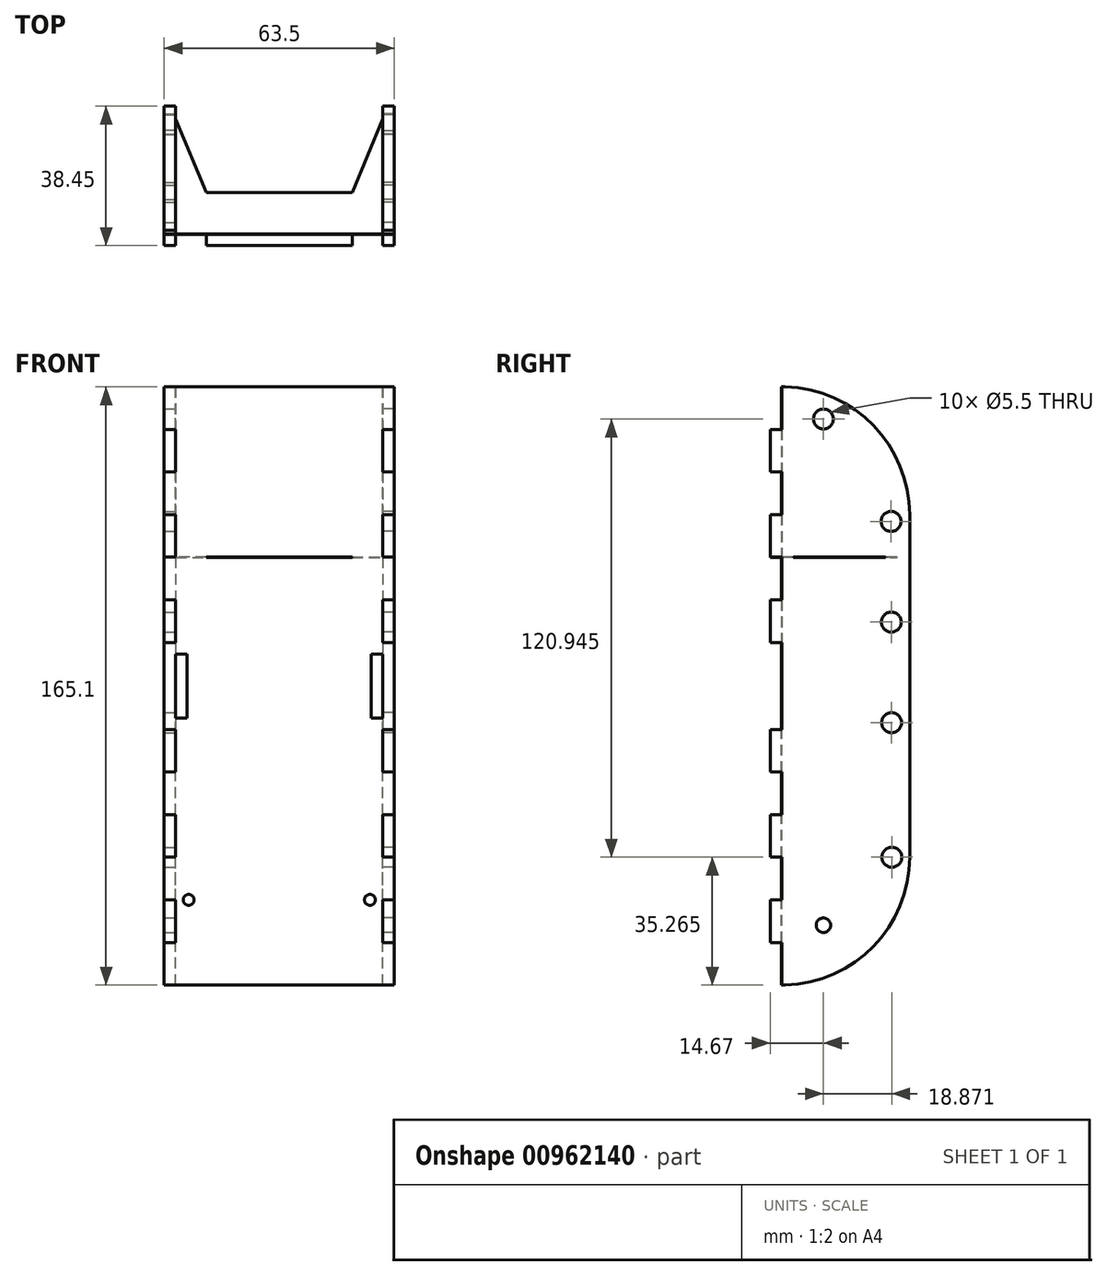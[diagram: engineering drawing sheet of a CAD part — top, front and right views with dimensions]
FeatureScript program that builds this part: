
annotation { "Feature Type Name" : "Feature", "Feature Type Description" : "" }
export const myFeature = defineFeature(function(context is Context, id is Id, definition is map)
    precondition{}
    {
        {
            assignVariable(context, id + "F0", {"name" : "Thickness", "anyValue" : .125});
        }
        {
            var Q0;
            Q0=qCreatedBy(makeId("Front.planeOp"),FACE);
            var sketch = newSketch(context, id + "F1", { "sketchPlane" : qUnion([Q0])});
            skLineSegment(sketch, "E0", {"start": v(0, 0) * mm, "end": v(0, 49.56) * mm, "construction": true});
            skLineSegment(sketch, "E1", {"start": v(0, 0) * mm, "end": v(-25, 0) * mm, "construction": true});
            skCircle(sketch, "E2", {"center": v(-25, 0) * mm, "radius": 1.5 * mm, "construction": true});
            skLineSegment(sketch, "E3", {"start": v(0, -7) * mm, "end": v(-39.83, -7) * mm, "construction": true});
            skLineSegment(sketch, "E4", {"start": v(0, 141.6) * mm, "end": v(-22.22, 141.6) * mm, "construction": true});
            skLineSegment(sketch, "E5", {"start": v(-22.23, 141.6) * mm, "end": v(-22.22, -23.51) * mm, "construction": true});
            skLineSegment(sketch, "E6", {"start": v(-22.22, -23.51) * mm, "end": v(0, -23.5) * mm, "construction": true});
            skSolve(sketch);
        }
        {
            var Q0;
            Q0=qCreatedBy(makeId("Right.planeOp"),FACE);
            var sketch = newSketch(context, id + "F2", { "sketchPlane" : qUnion([Q0])});
            skLineSegment(sketch, "E7", {"start": v(0, -7) * mm, "end": v(11.5, -7) * mm, "construction": true});
            skCircle(sketch, "E8", {"center": v(11.5, -7) * mm, "radius": 2 * mm});
            skCircle(sketch, "E9", {"center": v(11.5, 132.7) * mm, "radius": 2.75 * mm});
            skSolve(sketch);
        }
        {
            var Q0;
            Q0=qCreatedBy(makeId("Front.planeOp"),FACE);
            var sketch = newSketch(context, id + "F3", { "sketchPlane" : qUnion([Q0])});
            skLineSegment(sketch, "E10", {"start": v(0, 141.6) * mm, "end": v(-31.75, 141.6) * mm, "construction": true});
            skLineSegment(sketch, "E11", {"start": v(0, -23.51) * mm, "end": v(-31.75, -23.51) * mm});
            skLineSegment(sketch, "E12", {"start": v(-31.75, -23.51) * mm, "end": v(-31.75, -11.76) * mm});
            skLineSegment(sketch, "E13", {"start": v(-31.75, -11.76) * mm, "end": v(-28.57, -11.76) * mm});
            skLineSegment(sketch, "E14", {"start": v(-28.57, -11.76) * mm, "end": v(-28.57, 0) * mm});
            skLineSegment(sketch, "E15", {"start": v(-28.57, 0) * mm, "end": v(-31.75, 0) * mm});
            skLineSegment(sketch, "E16", {"start": v(0, -23.51) * mm, "end": v(0, 141.6) * mm, "construction": true});
            skLineSegment(sketch, "E17", {"start": v(0, 59.04) * mm, "end": v(-66.34, 59.04) * mm, "construction": true});
            skLineSegment(sketch, "E18", {"start": v(-31.75, 59.04) * mm, "end": v(-31.75, 47.02) * mm});
            skLineSegment(sketch, "E19.1.0.0", {"start": v(-28.57, 23.51) * mm, "end": v(-31.75, 23.51) * mm});
            skLineSegment(sketch, "E19.1.0.1", {"start": v(-28.57, 11.76) * mm, "end": v(-28.57, 23.51) * mm});
            skLineSegment(sketch, "E19.1.0.2", {"start": v(-31.75, 11.76) * mm, "end": v(-28.57, 11.76) * mm});
            skLineSegment(sketch, "E19.1.0.3", {"start": v(-31.75, 0) * mm, "end": v(-31.75, 11.76) * mm});
            skLineSegment(sketch, "E19.2.0.0", {"start": v(-28.58, 47.02) * mm, "end": v(-31.75, 47.02) * mm});
            skLineSegment(sketch, "E19.2.0.1", {"start": v(-28.57, 35.27) * mm, "end": v(-28.57, 47.02) * mm});
            skLineSegment(sketch, "E19.2.0.2", {"start": v(-31.75, 35.27) * mm, "end": v(-28.58, 35.27) * mm});
            skLineSegment(sketch, "E19.2.0.3", {"start": v(-31.75, 23.51) * mm, "end": v(-31.75, 35.27) * mm});
            skLineSegment(sketch, "E19.direction1", {"start": v(-31.75, -23.51) * mm, "end": v(-31.75, 0) * mm, "construction": true});
            skLineSegment(sketch, "E20.MirrorCS", {"start": v(-31.75, 141.6) * mm, "end": v(-31.75, 129.84) * mm});
            skLineSegment(sketch, "E21.MirrorCS", {"start": v(-28.57, 118.08) * mm, "end": v(-31.75, 118.08) * mm});
            skLineSegment(sketch, "E22.MirrorCS", {"start": v(-28.58, 71.06) * mm, "end": v(-31.75, 71.06) * mm});
            skLineSegment(sketch, "E23.MirrorCS", {"start": v(-31.75, 94.57) * mm, "end": v(-31.75, 82.81) * mm});
            skLineSegment(sketch, "E24.MirrorCS", {"start": v(-31.75, 118.08) * mm, "end": v(-31.75, 106.33) * mm});
            skLineSegment(sketch, "E25.MirrorCS", {"start": v(-31.75, 129.84) * mm, "end": v(-28.57, 129.84) * mm});
            skLineSegment(sketch, "E26.MirrorCS", {"start": v(-28.57, 129.84) * mm, "end": v(-28.57, 118.08) * mm});
            skLineSegment(sketch, "E27.MirrorCS", {"start": v(-28.57, 82.81) * mm, "end": v(-28.57, 71.06) * mm});
            skLineSegment(sketch, "E28.MirrorCS", {"start": v(-31.75, 82.81) * mm, "end": v(-28.58, 82.81) * mm});
            skLineSegment(sketch, "E29.MirrorCS", {"start": v(-31.75, 106.33) * mm, "end": v(-28.57, 106.33) * mm});
            skLineSegment(sketch, "E30.MirrorCS", {"start": v(-28.57, 106.33) * mm, "end": v(-28.57, 94.57) * mm});
            skLineSegment(sketch, "E31.MirrorCS", {"start": v(-28.57, 94.57) * mm, "end": v(-31.75, 94.57) * mm});
            skLineSegment(sketch, "E32.MirrorCS", {"start": v(0, 141.6) * mm, "end": v(-31.75, 141.6) * mm});
            skLineSegment(sketch, "E33.MirrorCS", {"start": v(-31.75, 59.04) * mm, "end": v(-31.75, 71.06) * mm});
            skLineSegment(sketch, "E34.bottom", {"start": v(-28.58, 67.89) * mm, "end": v(-25.4, 67.89) * mm});
            skLineSegment(sketch, "E34.top", {"start": v(-28.58, 50.2) * mm, "end": v(-25.4, 50.2) * mm});
            skLineSegment(sketch, "E34.left", {"start": v(-28.58, 67.89) * mm, "end": v(-28.58, 50.2) * mm});
            skLineSegment(sketch, "E34.right", {"start": v(-25.4, 67.89) * mm, "end": v(-25.4, 50.2) * mm});
            skPoint(sketch, "E35", {"position": v(-28.58, 59.04) * mm});
            skLineSegment(sketch, "E36.MirrorCS", {"start": v(28.57, 23.51) * mm, "end": v(31.75, 23.51) * mm});
            skLineSegment(sketch, "E37.MirrorCS", {"start": v(31.75, 35.27) * mm, "end": v(28.58, 35.27) * mm});
            skLineSegment(sketch, "E38.MirrorCS", {"start": v(28.58, 71.06) * mm, "end": v(31.75, 71.06) * mm});
            skLineSegment(sketch, "E39.MirrorCS", {"start": v(31.75, -23.51) * mm, "end": v(31.75, -11.76) * mm});
            skLineSegment(sketch, "E40.MirrorCS", {"start": v(28.57, 0) * mm, "end": v(31.75, 0) * mm});
            skLineSegment(sketch, "E41.MirrorCS", {"start": v(28.58, 67.89) * mm, "end": v(25.4, 67.89) * mm});
            skLineSegment(sketch, "E42.MirrorCS", {"start": v(31.75, 82.81) * mm, "end": v(28.58, 82.81) * mm});
            skLineSegment(sketch, "E43.MirrorCS", {"start": v(31.75, 59.04) * mm, "end": v(31.75, 71.06) * mm});
            skLineSegment(sketch, "E44.MirrorCS", {"start": v(31.75, 11.76) * mm, "end": v(28.57, 11.76) * mm});
            skLineSegment(sketch, "E45.MirrorCS", {"start": v(31.75, 94.57) * mm, "end": v(31.75, 82.81) * mm});
            skLineSegment(sketch, "E46.MirrorCS", {"start": v(31.75, 141.6) * mm, "end": v(31.75, 129.84) * mm});
            skLineSegment(sketch, "E47.MirrorCS", {"start": v(28.57, 94.57) * mm, "end": v(31.75, 94.57) * mm});
            skLineSegment(sketch, "E48.MirrorCS", {"start": v(31.75, 118.08) * mm, "end": v(31.75, 106.33) * mm});
            skLineSegment(sketch, "E49.MirrorCS", {"start": v(31.75, -11.76) * mm, "end": v(28.57, -11.76) * mm});
            skLineSegment(sketch, "E50.MirrorCS", {"start": v(28.57, 118.08) * mm, "end": v(31.75, 118.08) * mm});
            skLineSegment(sketch, "E51.MirrorCS", {"start": v(31.75, 23.51) * mm, "end": v(31.75, 35.27) * mm});
            skLineSegment(sketch, "E52.MirrorCS", {"start": v(28.57, -11.76) * mm, "end": v(28.57, 0) * mm});
            skLineSegment(sketch, "E53.MirrorCS", {"start": v(31.75, 129.84) * mm, "end": v(28.57, 129.84) * mm});
            skLineSegment(sketch, "E54.MirrorCS", {"start": v(28.58, 67.89) * mm, "end": v(28.58, 50.2) * mm});
            skLineSegment(sketch, "E55.MirrorCS", {"start": v(28.58, 47.02) * mm, "end": v(31.75, 47.02) * mm});
            skLineSegment(sketch, "E56.MirrorCS", {"start": v(28.57, 35.27) * mm, "end": v(28.57, 47.02) * mm});
            skLineSegment(sketch, "E57.MirrorCS", {"start": v(31.75, 0) * mm, "end": v(31.75, 11.76) * mm});
            skLineSegment(sketch, "E58.MirrorCS", {"start": v(31.75, 59.04) * mm, "end": v(31.75, 47.02) * mm});
            skLineSegment(sketch, "E59.MirrorCS", {"start": v(28.57, 11.76) * mm, "end": v(28.57, 23.51) * mm});
            skLineSegment(sketch, "E60.MirrorCS", {"start": v(28.58, 50.2) * mm, "end": v(25.4, 50.2) * mm});
            skLineSegment(sketch, "E61.MirrorCS", {"start": v(31.75, 106.33) * mm, "end": v(28.57, 106.33) * mm});
            skLineSegment(sketch, "E62.MirrorCS", {"start": v(28.57, 82.81) * mm, "end": v(28.57, 71.06) * mm});
            skLineSegment(sketch, "E63.MirrorCS", {"start": v(28.57, 129.84) * mm, "end": v(28.57, 118.08) * mm});
            skLineSegment(sketch, "E64.MirrorCS", {"start": v(28.57, 106.33) * mm, "end": v(28.57, 94.57) * mm});
            skLineSegment(sketch, "E65.MirrorCS", {"start": v(0, 141.6) * mm, "end": v(31.75, 141.6) * mm});
            skLineSegment(sketch, "E66.MirrorCS", {"start": v(25.4, 67.89) * mm, "end": v(25.4, 50.2) * mm});
            skLineSegment(sketch, "E67.MirrorCS", {"start": v(0, 141.6) * mm, "end": v(31.75, 141.6) * mm, "construction": true});
            skLineSegment(sketch, "E68.MirrorCS", {"start": v(0, -23.51) * mm, "end": v(31.75, -23.51) * mm});
            skPoint(sketch, "E69.MirrorP", {"position": v(28.58, 59.04) * mm});
            skCircle(sketch, "E70", {"center": v(-25, 0) * mm, "radius": 1.5 * mm});
            skCircle(sketch, "E71.MirrorC", {"center": v(25, 0) * mm, "radius": 1.5 * mm});
            skSolve(sketch);
        }
        {
            var Q0;
            Q0=makeQuery(id+"F3.imprint","IMPRINT",FACE,{"disambiguationData":[TD([[makeQuery(id+"F3.imprint","IMPRINT",EDGE,{"derivedFrom":sQuery(id+"F3.wireOp",EDGE,"E11")}),-1.0]])]});
            extrude(context, id + "F4", {"entities" : qUnion([Q0]), "depth" : (getVariable(context, 'Thickness')) * mm, "offsetDistance" : 25.4 * mm});
        }
        {
            var Q0;
            Q0=qCreatedBy(makeId("Right.planeOp"),FACE);
            var sketch = newSketch(context, id + "F5", { "sketchPlane" : qUnion([Q0])});
            skLineSegment(sketch, "E72", {"start": v(0, -23.51) * mm, "end": v(0, -11.76) * mm});
            skLineSegment(sketch, "E73", {"start": v(0, -11.76) * mm, "end": v(-3.18, -11.76) * mm});
            skLineSegment(sketch, "E74", {"start": v(-3.18, -11.76) * mm, "end": v(-3.18, 0) * mm});
            skLineSegment(sketch, "E75", {"start": v(-3.18, 0) * mm, "end": v(0, 0) * mm});
            skLineSegment(sketch, "E76.1.0.0", {"start": v(0, 0) * mm, "end": v(0, 11.75) * mm});
            skLineSegment(sketch, "E76.1.0.1", {"start": v(0, 11.76) * mm, "end": v(-3.18, 11.75) * mm});
            skLineSegment(sketch, "E76.1.0.2", {"start": v(-3.18, 11.75) * mm, "end": v(-3.18, 23.51) * mm});
            skLineSegment(sketch, "E76.1.0.3", {"start": v(-3.18, 23.51) * mm, "end": v(0, 23.51) * mm});
            skLineSegment(sketch, "E76.2.0.0", {"start": v(0, 23.51) * mm, "end": v(0, 35.27) * mm});
            skLineSegment(sketch, "E76.2.0.1", {"start": v(0, 35.27) * mm, "end": v(-3.17, 35.27) * mm});
            skLineSegment(sketch, "E76.2.0.2", {"start": v(-3.17, 35.27) * mm, "end": v(-3.17, 47.02) * mm});
            skLineSegment(sketch, "E76.2.0.3", {"start": v(-3.17, 47.02) * mm, "end": v(0, 47.02) * mm});
            skLineSegment(sketch, "E76.direction1", {"start": v(0, -23.51) * mm, "end": v(0, 0) * mm, "construction": true});
            skLineSegment(sketch, "E77", {"start": v(-17.44, 59.04) * mm, "end": v(0, 59.04) * mm, "construction": true});
            skLineSegment(sketch, "E78", {"start": v(0, 47.02) * mm, "end": v(0, 59.04) * mm});
            skLineSegment(sketch, "E79.MirrorCS", {"start": v(-3.18, 118.08) * mm, "end": v(0, 118.08) * mm});
            skLineSegment(sketch, "E80.MirrorCS", {"start": v(0, 82.82) * mm, "end": v(-3.17, 82.82) * mm});
            skLineSegment(sketch, "E81.MirrorCS", {"start": v(-3.18, 94.57) * mm, "end": v(0, 94.57) * mm});
            skLineSegment(sketch, "E82.MirrorCS", {"start": v(0, 129.84) * mm, "end": v(-3.18, 129.84) * mm});
            skLineSegment(sketch, "E83.MirrorCS", {"start": v(-3.17, 71.06) * mm, "end": v(0, 71.06) * mm});
            skLineSegment(sketch, "E84.MirrorCS", {"start": v(0, 106.33) * mm, "end": v(-3.18, 106.33) * mm});
            skLineSegment(sketch, "E85.MirrorCS", {"start": v(0, 141.6) * mm, "end": v(0, 129.84) * mm});
            skLineSegment(sketch, "E86.MirrorCS", {"start": v(0, 141.6) * mm, "end": v(0, 118.08) * mm, "construction": true});
            skLineSegment(sketch, "E87.MirrorCS", {"start": v(-3.18, 106.33) * mm, "end": v(-3.18, 94.57) * mm});
            skLineSegment(sketch, "E88.MirrorCS", {"start": v(0, 118.08) * mm, "end": v(0, 106.33) * mm});
            skLineSegment(sketch, "E89.MirrorCS", {"start": v(-3.17, 82.82) * mm, "end": v(-3.17, 71.06) * mm});
            skLineSegment(sketch, "E90.MirrorCS", {"start": v(0, 71.06) * mm, "end": v(0, 59.04) * mm});
            skLineSegment(sketch, "E91.MirrorCS", {"start": v(0, 94.57) * mm, "end": v(0, 82.82) * mm});
            skLineSegment(sketch, "E92.MirrorCS", {"start": v(-3.18, 129.84) * mm, "end": v(-3.18, 118.08) * mm});
            skCircle(sketch, "E93", {"center": v(11.5, 132.7) * mm, "radius": 2.75 * mm});
            skCircle(sketch, "E94", {"center": v(11.5, -7) * mm, "radius": 2 * mm});
            skCircle(sketch, "E95", {"center": v(11.5, 132.7) * mm, "radius": 16 * mm, "construction": true});
            skCircle(sketch, "E96", {"center": v(11.5, -7) * mm, "radius": 16 * mm, "construction": true});
            skCircle(sketch, "E97", {"center": v(30.37, 21.12) * mm, "radius": 11 * mm, "construction": true});
            skCircle(sketch, "E98", {"center": v(30.16, 104.44) * mm, "radius": 11 * mm, "construction": true});
            skLineSegment(sketch, "E99", {"start": v(41.16, 104.47) * mm, "end": v(41.37, 21.15) * mm, "construction": true});
            skCircle(sketch, "E100.1.0.0", {"center": v(30.23, 76.67) * mm, "radius": 11 * mm, "construction": true});
            skCircle(sketch, "E100.2.0.0", {"center": v(30.3, 48.9) * mm, "radius": 11 * mm, "construction": true});
            skLineSegment(sketch, "E100.direction1", {"start": v(30.16, 104.44) * mm, "end": v(30.23, 76.67) * mm, "construction": true});
            skCircle(sketch, "E101", {"center": v(30.16, 104.44) * mm, "radius": 2.75 * mm});
            skCircle(sketch, "E102", {"center": v(30.23, 76.67) * mm, "radius": 2.75 * mm});
            skCircle(sketch, "E103", {"center": v(30.3, 48.9) * mm, "radius": 2.75 * mm});
            skArc(sketch, "E104", {"start": v(0.97, -23.51) * mm, "mid": v(25.29, -12.85) * mm, "end": v(35.28, 11.75) * mm});
            skArc(sketch, "E105.MirrorCS", {"start": v(0.97, 141.6) * mm, "mid": v(25.29, 130.93) * mm, "end": v(35.28, 106.33) * mm});
            skLineSegment(sketch, "E106", {"start": v(35.28, 11.76) * mm, "end": v(35.28, 106.33) * mm});
            skLineSegment(sketch, "E107", {"start": v(0.97, 141.6) * mm, "end": v(0, 141.6) * mm});
            skLineSegment(sketch, "E108", {"start": v(0.97, -23.51) * mm, "end": v(0, -23.51) * mm});
            skLineSegment(sketch, "E109", {"start": v(26.06, 139.33) * mm, "end": v(40.92, 106.72) * mm, "construction": true});
            skLineSegment(sketch, "E110", {"start": v(39.72, 15.32) * mm, "end": v(25.97, -13.82) * mm, "construction": true});
            skCircle(sketch, "E111", {"center": v(30.37, 11.76) * mm, "radius": 2.75 * mm});
            skLineSegment(sketch, "E112", {"start": v(35.28, 11.75) * mm, "end": v(0, 11.75) * mm, "construction": true});
            skLineSegment(sketch, "E113", {"start": v(33.3, 11.76) * mm, "end": v(44.3, 11.8) * mm, "construction": true});
            skArc(sketch, "E114", {"start": v(44.3, 11.8) * mm, "mid": v(16.45, 12.05) * mm, "end": v(44.28, 11.13) * mm, "construction": true});
            skSolve(sketch);
        }
        {
            var Q0;
            Q0=makeQuery(id+"F5.imprint","IMPRINT",FACE,{"disambiguationData":[TD([[makeQuery(id+"F5.imprint","IMPRINT",EDGE,{"derivedFrom":sQuery(id+"F5.wireOp",EDGE,"E72")}),-1.0]])]});
            var Q1;
            Q1=makeQuery(id+"F4.opExtrude","CAP_VERTEX",VERTEX,{"disambiguationData":[OSD([sQuery(id+"F3.wireOp",EDGE,"E46.MirrorCS"),sQuery(id+"F3.wireOp",EDGE,"E65.MirrorCS")])],"isStart":false});
            var Q2;
            Q2=makeQuery(id+"F4.opExtrude","CAP_VERTEX",VERTEX,{"disambiguationData":[OSD([sQuery(id+"F3.wireOp",EDGE,"E53.MirrorCS"),sQuery(id+"F3.wireOp",EDGE,"E63.MirrorCS")])],"isStart":true});
            extrude(context, id + "F6", {"entities" : qUnion([Q0]), "endBound" : BoundingType.UP_TO_VERTEX, "depth" : 25.4 * mm, "endBoundEntityVertex" : qUnion([Q1]), "offsetDistance" : 25.4 * mm, "hasSecondDirection" : true, "secondDirectionBound" : SecondDirectionBoundingType.UP_TO_VERTEX, "secondDirectionOppositeDirection" : false, "secondDirectionDepth" : 25.4 * mm, "secondDirectionBoundEntityVertex" : qUnion([Q2])});
        }
        {
            var Q0;
            Q0=makeQuery(id+"F6.opExtrude","SWEPT_BODY",BODY,{"disambiguationData":[OSD([sQuery(id+"F5.wireOp",EDGE,"E72"),sQuery(id+"F5.wireOp",EDGE,"E73"),sQuery(id+"F5.wireOp",EDGE,"E74"),sQuery(id+"F5.wireOp",EDGE,"E75"),sQuery(id+"F5.wireOp",EDGE,"E76.1.0.0"),sQuery(id+"F5.wireOp",EDGE,"E76.1.0.1"),sQuery(id+"F5.wireOp",EDGE,"E76.1.0.2"),sQuery(id+"F5.wireOp",EDGE,"E76.1.0.3"),sQuery(id+"F5.wireOp",EDGE,"E76.2.0.0"),sQuery(id+"F5.wireOp",EDGE,"E76.2.0.1"),sQuery(id+"F5.wireOp",EDGE,"E76.2.0.2"),sQuery(id+"F5.wireOp",EDGE,"E76.2.0.3"),sQuery(id+"F5.wireOp",EDGE,"E78"),sQuery(id+"F5.wireOp",EDGE,"E79.MirrorCS"),sQuery(id+"F5.wireOp",EDGE,"E80.MirrorCS"),sQuery(id+"F5.wireOp",EDGE,"E81.MirrorCS"),sQuery(id+"F5.wireOp",EDGE,"E82.MirrorCS"),sQuery(id+"F5.wireOp",EDGE,"E83.MirrorCS"),sQuery(id+"F5.wireOp",EDGE,"E84.MirrorCS"),sQuery(id+"F5.wireOp",EDGE,"E85.MirrorCS"),sQuery(id+"F5.wireOp",EDGE,"E87.MirrorCS"),sQuery(id+"F5.wireOp",EDGE,"E88.MirrorCS"),sQuery(id+"F5.wireOp",EDGE,"E89.MirrorCS"),sQuery(id+"F5.wireOp",EDGE,"E90.MirrorCS"),sQuery(id+"F5.wireOp",EDGE,"E91.MirrorCS"),sQuery(id+"F5.wireOp",EDGE,"E92.MirrorCS"),sQuery(id+"F5.wireOp",EDGE,"0A0D79Jb-YNL0-oHs5-xmzd-RRcL05y1tXJ9"),sQuery(id+"F5.wireOp",EDGE,"80kzLmsw-Zs1p-2aaz-TAWa-7CPWT32ig2Pu"),sQuery(id+"F5.wireOp",EDGE,"pLrTUgb4-zpkk-BDbY-rqmu-NSZ4KMZ8J1Q6"),sQuery(id+"F5.wireOp",EDGE,"f717e129-c6dc-423f-bb26-04237818bbe8"),sQuery(id+"F5.wireOp",EDGE,"E93"),sQuery(id+"F5.wireOp",EDGE,"E94"),sQuery(id+"F5.wireOp",EDGE,"708f4e70-830a-4111-bdb2-f223d600d2c5")])]});
            var Q1;
            Q1=qCreatedBy(makeId("Right.planeOp"),FACE);
            mirror(context, id + "F7", {"entities" : qUnion([Q0]), "mirrorPlane" : qUnion([Q1])});
        }
        {
            var Q0;
            Q0=qCreatedBy(makeId("Top.planeOp"),FACE);
            var sketch = newSketch(context, id + "F8", { "sketchPlane" : qUnion([Q0])});
            skLineSegment(sketch, "E115", {"start": v(0, 11.5) * mm, "end": v(-20.1, 11.5) * mm});
            skLineSegment(sketch, "E116", {"start": v(-20.1, 11.5) * mm, "end": v(-28.57, 31.75) * mm});
            skLineSegment(sketch, "E117", {"start": v(-28.57, 31.75) * mm, "end": v(-28.57, 28.57) * mm});
            skLineSegment(sketch, "E118", {"start": v(-28.57, 28.57) * mm, "end": v(-31.75, 28.57) * mm});
            skLineSegment(sketch, "E119", {"start": v(-31.75, 28.58) * mm, "end": v(-31.75, 3.17) * mm});
            skLineSegment(sketch, "E120", {"start": v(-31.75, 3.17) * mm, "end": v(-28.57, 3.17) * mm});
            skLineSegment(sketch, "E121", {"start": v(-28.57, 3.18) * mm, "end": v(-28.57, 0) * mm});
            skLineSegment(sketch, "E122", {"start": v(-28.57, 0) * mm, "end": v(-20.1, 0) * mm});
            skLineSegment(sketch, "E123", {"start": v(-20.1, 0) * mm, "end": v(-20.1, -3.18) * mm});
            skLineSegment(sketch, "E124", {"start": v(-20.1, -3.18) * mm, "end": v(0, -3.18) * mm});
            skLineSegment(sketch, "E125", {"start": v(0, -3.18) * mm, "end": v(0, 11.5) * mm, "construction": true});
            skLineSegment(sketch, "E126.MirrorCS", {"start": v(20.1, 0) * mm, "end": v(20.1, -3.18) * mm});
            skLineSegment(sketch, "E127.MirrorCS", {"start": v(28.57, 3.17) * mm, "end": v(28.57, 0) * mm});
            skLineSegment(sketch, "E128.MirrorCS", {"start": v(28.57, 0) * mm, "end": v(20.1, 0) * mm});
            skLineSegment(sketch, "E129.MirrorCS", {"start": v(28.57, 31.75) * mm, "end": v(28.57, 28.58) * mm});
            skLineSegment(sketch, "E130.MirrorCS", {"start": v(28.57, 28.58) * mm, "end": v(31.75, 28.58) * mm});
            skLineSegment(sketch, "E131.MirrorCS", {"start": v(31.75, 3.17) * mm, "end": v(28.57, 3.17) * mm});
            skLineSegment(sketch, "E132.MirrorCS", {"start": v(0, 11.5) * mm, "end": v(20.1, 11.5) * mm});
            skLineSegment(sketch, "E133.MirrorCS", {"start": v(20.1, -3.18) * mm, "end": v(0, -3.18) * mm});
            skLineSegment(sketch, "E134.MirrorCS", {"start": v(20.1, 11.5) * mm, "end": v(28.57, 31.75) * mm});
            skLineSegment(sketch, "E135.MirrorCS", {"start": v(31.75, 28.58) * mm, "end": v(31.75, 3.18) * mm});
            skSolve(sketch);
        }
        {
            var Q0;
            Q0=qSketchRegion(id+"F8",true);
            var Q1;
            Q1=makeQuery(id+"F4.opExtrude","CAP_VERTEX",VERTEX,{"disambiguationData":[OSD([sQuery(id+"F3.wireOp",EDGE,"E23.MirrorCS"),sQuery(id+"F3.wireOp",EDGE,"E31.MirrorCS")])],"isStart":true});
            var Q2;
            Q2=makeQuery(id+"F4.opExtrude","CAP_VERTEX",VERTEX,{"disambiguationData":[OSD([sQuery(id+"F3.wireOp",EDGE,"E23.MirrorCS"),sQuery(id+"F3.wireOp",EDGE,"E31.MirrorCS")])],"isStart":true});
            extrude(context, id + "F9", {"entities" : qUnion([Q0]), "operationType" : NewBodyOperationType.REMOVE, "endBound" : BoundingType.UP_TO_VERTEX, "depth" : 25.4 * mm, "endBoundEntityVertex" : qUnion([Q1]), "offsetDistance" : 25.4 * mm, "hasSecondDirection" : true, "secondDirectionBound" : SecondDirectionBoundingType.UP_TO_VERTEX, "secondDirectionOppositeDirection" : false, "secondDirectionDepth" : 25.4 * mm, "secondDirectionBoundEntityVertex" : qUnion([Q2]), "hasSecondDirectionOffset" : true, "secondDirectionOffsetDistance" : (getVariable(context, 'Thickness')) * mm});
        }
        {
            var Q0;
            Q0=qSketchRegion(id+"F8",true);
            var Q1;
            Q1=makeQuery(id+"F4.opExtrude","CAP_VERTEX",VERTEX,{"disambiguationData":[OSD([sQuery(id+"F3.wireOp",EDGE,"E23.MirrorCS"),sQuery(id+"F3.wireOp",EDGE,"E31.MirrorCS")])],"isStart":true});
            var Q2;
            Q2=makeQuery(id+"F4.opExtrude","CAP_VERTEX",VERTEX,{"disambiguationData":[OSD([sQuery(id+"F3.wireOp",EDGE,"E23.MirrorCS"),sQuery(id+"F3.wireOp",EDGE,"E31.MirrorCS")])],"isStart":true});
            extrude(context, id + "F10", {"entities" : qUnion([Q0]), "endBound" : BoundingType.UP_TO_VERTEX, "depth" : 25.4 * mm, "endBoundEntityVertex" : qUnion([Q1]), "offsetDistance" : 25.4 * mm, "hasSecondDirection" : true, "secondDirectionBound" : SecondDirectionBoundingType.UP_TO_VERTEX, "secondDirectionOppositeDirection" : false, "secondDirectionDepth" : 25.4 * mm, "secondDirectionBoundEntityVertex" : qUnion([Q2]), "hasSecondDirectionOffset" : true, "secondDirectionOffsetDistance" : (getVariable(context, 'Thickness')) * mm});
        }
    });
